# Revit family: ПАС300_30.06.2021
name_source: partatom
category: Оборудование
units: mm (PartAtom-declared; Revit-internal decimal feet)

## family parameters
Всегда вертикально = Да
Классификация = Нет
На основе рабочей плоскости = Нет
Общий = Нет
При загрузке вырезать с полостями = Нет
Размер круглого соединителя = Использовать диаметр
Тип детали = Нормальный
Точка расчета площади = Нет

## types (1)
- ПАС300
    Высота = 107 мм
    Глубина = 33 мм
    Отметка по умолчанию = 0 мм
    Светодиод RS-485 = Да
    Светодиод МС302Р = Нет
    Светодиод Работа = Да
    Светодиод С300 = Да
    Светодиод С300-МС322 = Нет
    Светодиод ШЛЕЙФ 1 = Нет
    Текст RS-485 = Да
    Текст МС322 = Нет
    Текст Модуль МС302Р = Нет
    Текст ПАС300 = Да
    Текст Работа = Да
    Текст С300 = Да
    Текст С300 - МС322 = Нет
    Текст Устройство 1 = Нет
    Текст Устройство 2 = Нет
    Текст ШЛЕЙФ 1 = Нет
    Текст ШЛЕЙФ 2 = Нет
    Ширина = 156 мм
    коннект Мощ Сб = Да
    коннект Мощ сб2 = Да
    коннект ПС = Да
    коннект ПС2 = Да
    коннект ПУ = Да
    коннект ПУ2 = Да
    коннект Упр = Да
    коннект Упр2 = Нет
